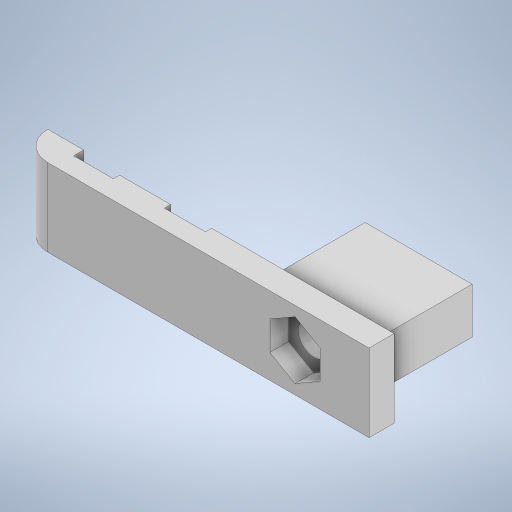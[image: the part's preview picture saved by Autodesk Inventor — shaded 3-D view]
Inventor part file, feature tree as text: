
AUTODESK INVENTOR PART (.ipt)
format: ipt  version: 2023.3 (Build 273359000, 359)  size: 370,688 bytes
history: native  units: in
note: dims shown in document units (in); Inventor stores cm internally (conversion verified against a paired STEP export)
features: reference x9, extrude x6, sketch x4, other x3, fillet x1, projected_geometry x1
ambient origin geometry x8: Origin, YZ Plane, XZ Plane, XY Plane, X Axis, Y Axis, Z Axis, Center Point
bodies: Solid1 (feature_tree)
feature tree (24):
  extrude  "side"  Depth=0.0787in
  extrude  "sliding_block"  Depth=0.0067in
  extrude  "hole"  Depth=0.311in TaperAngle=0.0deg
  extrude  "alignment_cut"  Depth=0.0197in TaperAngle=0.0deg
  sketch  "Sketch5"  dims[d10=0.3937in d11=0.0in d12=0.0197in d13=0.0in d17=0.0118in d18=0.0in d19=0.1575in d20=0.0591in d21=0.0in d22=0.0906in d25=0.0067in]
  extrude  "probe_slot"  Depth=0.0118in TaperAngle=0.0deg
  extrude  "nut_slot"  Depth=0.1575in TaperAngle=0.0deg
  fillet  "Fillet3"  Radius=0.0906in
  sketch  "Sketch2"  dims[d0=0.0787in d1=0.0in d2=0.0067in]
  reference  "Reference6"
  sketch  "Sketch3"  dims[d4=0.0067in d5=0.0067in]
  sketch  "Sketch4"  dims[d6=0.0984in d7=0.311in d8=0.0in]
  reference  "Reference24"
  reference  "Reference25"
  reference  "Reference27"
  reference  "Reference29"
  projected_geometry  "Projected Loop1"
  reference  "Reference31"
  reference  "Reference34"
  reference  "Reference38"
  reference  "Reference39"
  parser-record x1  (decoder bookkeeping rows leaked as tree rows — omitted from the tree; the rows remain in map.json)
  other  "np2a_assembly.iam"
  other  "stereotax_main:1"
note: 1 file-system path scrubbed to <path> (originals preserved in map.json)
